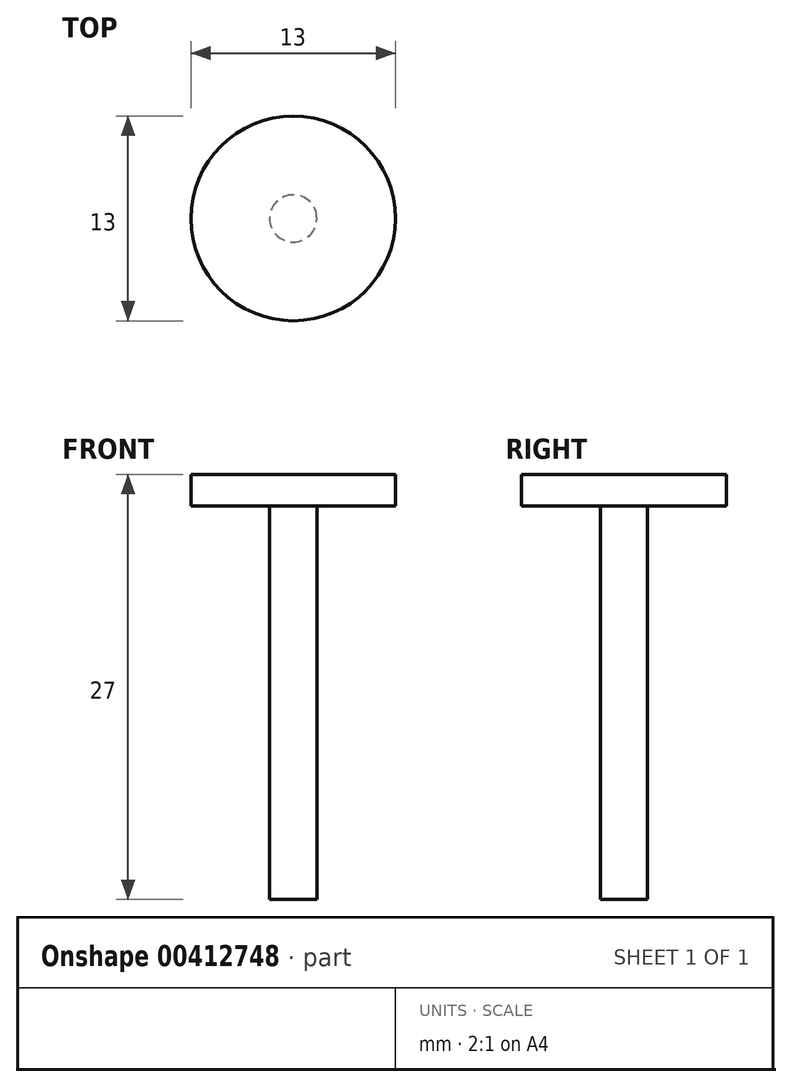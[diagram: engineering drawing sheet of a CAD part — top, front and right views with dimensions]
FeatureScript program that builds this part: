
annotation { "Feature Type Name" : "Feature", "Feature Type Description" : "" }
export const myFeature = defineFeature(function(context is Context, id is Id, definition is map)
    precondition{}
    {
        {
            var Q0;
            Q0=qCreatedBy(makeId("Top.planeOp"),FACE);
            var sketch = newSketch(context, id + "F0", { "sketchPlane" : qUnion([Q0])});
            skCircle(sketch, "E0", {"center": v(0, 0) * mm, "radius": 1.5 * mm});
            skSolve(sketch);
        }
        {
            var Q0;
            Q0 = qSketchRegion(id + "F0", true);
            extrude(context, id + "F1", {"entities" : qUnion([Q0]), "depth" : 25 * mm});
        }
        {
            var Q0;
            Q0=makeQuery(id+"F1.opExtrude","CAP_FACE",FACE,{"disambiguationData":[OSD([sQuery(id+"F0.wireOp",EDGE,"E0")])],"isStart":false});
            var sketch = newSketch(context, id + "F2", { "sketchPlane" : qUnion([Q0])});
            skCircle(sketch, "E1", {"center": v(0, 0) * mm, "radius": 6.5 * mm});
            skSolve(sketch);
        }
        {
            var Q0;
            Q0=makeQuery(id+"F2.imprint","IMPRINT",FACE,{"disambiguationData":[TD([[makeQuery(id+"F2.imprint","IMPRINT",EDGE,{"derivedFrom":sQuery(id+"F2.wireOp",EDGE,"E1")}),1.0]])]});
            var Q1;
            Q1=makeQuery(id+"F2.imprint","IMPRINT",FACE,{"disambiguationData":[TD([[makeQuery(id+"F2.imprint","IMPRINT",EDGE,{"derivedFrom":makeQuery(id+"F1.opExtrude","CAP_EDGE",EDGE,{"disambiguationData":[OSD([sQuery(id+"F0.wireOp",EDGE,"E0")])],"isStart":false})}),1.0]])]});
            extrude(context, id + "F3", {"entities" : qUnion([Q0, Q1]), "depth" : 2 * mm});
        }
    });
